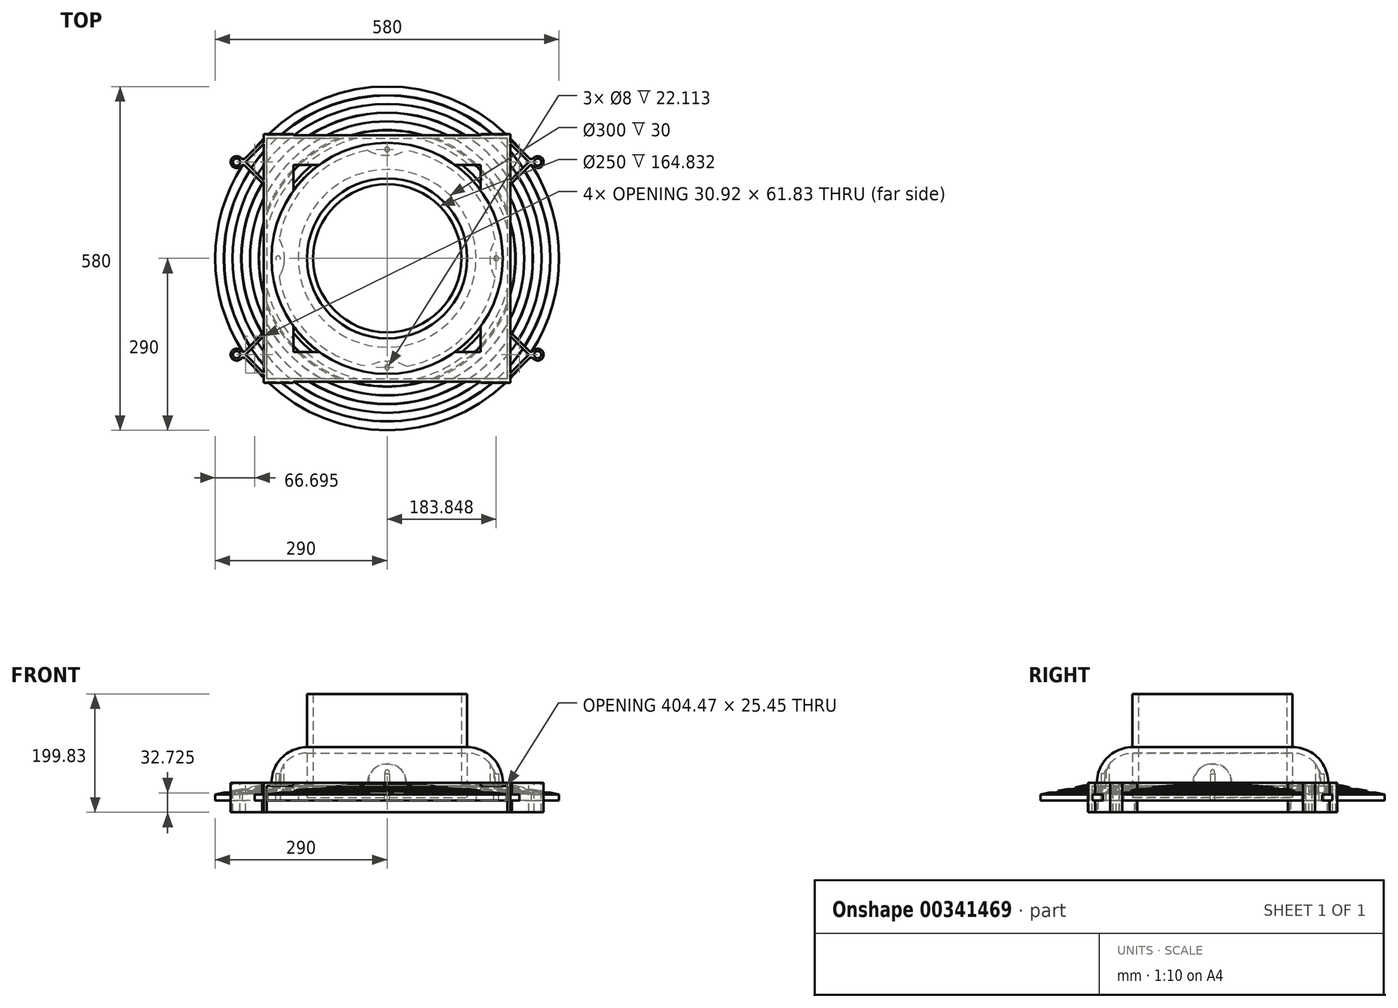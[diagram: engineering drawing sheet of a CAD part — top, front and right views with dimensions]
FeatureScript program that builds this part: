
annotation { "Feature Type Name" : "Feature", "Feature Type Description" : "" }
export const myFeature = defineFeature(function(context is Context, id is Id, definition is map)
    precondition{}
    {
        {
            var Q0;
            Q0=qCreatedBy(makeId("Top.planeOp"),FACE);
            var sketch = newSketch(context, id + "F0", { "sketchPlane" : qUnion([Q0])});
            skCircle(sketch, "E0", {"center": v(0, 0) * mm, "radius": 195 * mm});
            skCircle(sketch, "E1", {"center": v(0, 0) * mm, "radius": 135 * mm});
            skCircle(sketch, "E2", {"center": v(-183.85, 0) * mm, "radius": 4 * mm});
            skCircle(sketch, "E3", {"center": v(0, -183.85) * mm, "radius": 4 * mm});
            skCircle(sketch, "E4", {"center": v(183.85, 0) * mm, "radius": 4 * mm});
            skCircle(sketch, "E5", {"center": v(0, 183.85) * mm, "radius": 4 * mm});
            skFitSpline(sketch, "E6.MirrorCS", {"points": [v(-182.1, 32.59) * mm, v(-173.85, 0) * mm, v(-182.37, -31.1) * mm], "startDerivative": vector(43.9, -86.79) * mm, "endDerivative": vector(-46.42, -79.56) * mm});
            skArc(sketch, "E7.trimOffspring", {"start": v(-182.1, 32.59) * mm, "mid": v(-185, 0.76) * mm, "end": v(-182.37, -31.1) * mm});
            skArc(sketch, "E8.MirrorCS", {"start": v(32.59, -182.1) * mm, "mid": v(0.76, -185) * mm, "end": v(-31.1, -182.37) * mm});
            skFitSpline(sketch, "E9.MirrorCS", {"points": [v(32.59, -182.1) * mm, v(0, -173.85) * mm, v(-31.1, -182.37) * mm], "startDerivative": vector(-86.79, 43.9) * mm, "endDerivative": vector(-79.56, -46.42) * mm});
            skFitSpline(sketch, "E10.MirrorCS", {"points": [v(-32.59, 182.1) * mm, v(0, 173.85) * mm, v(31.1, 182.37) * mm], "startDerivative": vector(86.79, -43.9) * mm, "endDerivative": vector(79.56, 46.42) * mm});
            skArc(sketch, "E11.MirrorCS", {"start": v(-32.59, 182.1) * mm, "mid": v(-0.76, 185) * mm, "end": v(31.1, 182.37) * mm});
            skFitSpline(sketch, "E12.MirrorCS", {"points": [v(182.1, -32.59) * mm, v(173.85, 0) * mm, v(182.37, 31.1) * mm], "startDerivative": vector(-43.9, 86.79) * mm, "endDerivative": vector(46.42, 79.56) * mm});
            skArc(sketch, "E13.MirrorCS", {"start": v(182.1, -32.59) * mm, "mid": v(185, -0.76) * mm, "end": v(182.37, 31.1) * mm});
            skSolve(sketch);
        }
        {
            var Q0;
            Q0=qCreatedBy(makeId("Front.planeOp"),FACE);
            var sketch = newSketch(context, id + "F1", { "sketchPlane" : qUnion([Q0])});
            skLineSegment(sketch, "E14.top", {"start": v(195, 0) * mm, "end": v(185, 0) * mm});
            skLineSegment(sketch, "E15", {"start": v(135, -25) * mm, "end": v(135, 50) * mm});
            skLineSegment(sketch, "E16", {"start": v(185, 0) * mm, "end": v(135, 0) * mm, "construction": true});
            skArc(sketch, "E17", {"start": v(195, 0) * mm, "mid": v(177.43, 42.43) * mm, "end": v(135, 60) * mm});
            skArc(sketch, "E18", {"start": v(185, 0) * mm, "mid": v(170.36, 35.36) * mm, "end": v(135, 50) * mm});
            skLineSegment(sketch, "E19", {"start": v(135, 50) * mm, "end": v(135, 60) * mm, "construction": true});
            skLineSegment(sketch, "E20", {"start": v(135, 60) * mm, "end": v(135, 149.83) * mm});
            skLineSegment(sketch, "E21", {"start": v(135, 149.83) * mm, "end": v(125, 149.83) * mm});
            skLineSegment(sketch, "E22", {"start": v(125, 149.83) * mm, "end": v(125, -15) * mm});
            skLineSegment(sketch, "E23", {"start": v(0, -25) * mm, "end": v(135, -25) * mm});
            skLineSegment(sketch, "E24", {"start": v(0, -25) * mm, "end": v(0, -15) * mm});
            skLineSegment(sketch, "E25", {"start": v(0, -15) * mm, "end": v(125, -15) * mm});
            skSolve(sketch);
        }
        {
            var Q0;
            Q0=qSketchRegion(id+"F1",true);
            var Q1;
            Q1=sQuery(id+"F1.wireOp",EDGE,"E24");
            revolve(context, id + "F2", {"entities" : qUnion([Q0]), "axis" : qUnion([Q1]), "revolveType" : RevolveType.FULL});
        }
        {
            var Q0;
            {var subQ4=sQuery(id+"F0.wireOp",EDGE,"E6.MirrorCS");Q0=makeQuery(id+"F0.imprint","IMPRINT",FACE,{"disambiguationData":[TD([[makeQuery(id+"F0.imprint","IMPRINT",EDGE,{"derivedFrom":subQ4}),-1.0]])]});}
            var Q1;
            {var subQ0=sQuery(id+"F0.wireOp",EDGE,"E7.trimOffspring");var subQ1=sQuery(id+"F0.wireOp",EDGE,"E2");var subQ2=makeQuery(id+"F0.imprint","INTERSECT",VERTEX,{"disambiguationData":[OD(0.0)],"derivedFrom":[subQ1,subQ0]});Q1=makeQuery(id+"F0.imprint","IMPRINT",FACE,{"disambiguationData":[TD([[makeQuery(id+"F0.imprint","IMPRINT",EDGE,{"disambiguationData":[TD([[subQ2,1.0]])],"derivedFrom":subQ1}),1.0]])]});}
            var Q2;
            {var subQ4=sQuery(id+"F0.wireOp",EDGE,"E9.MirrorCS");Q2=makeQuery(id+"F0.imprint","IMPRINT",FACE,{"disambiguationData":[TD([[makeQuery(id+"F0.imprint","IMPRINT",EDGE,{"derivedFrom":subQ4}),1.0]])]});}
            var Q3;
            {var subQ0=sQuery(id+"F0.wireOp",EDGE,"7527a271-581c-4256-96df-404e9d61ec270.MirrorCS");var subQ1=sQuery(id+"F0.wireOp",EDGE,"E3");var subQ2=makeQuery(id+"F0.imprint","INTERSECT",VERTEX,{"disambiguationData":[OD(0.0)],"derivedFrom":[subQ1,subQ0]});Q3=makeQuery(id+"F0.imprint","IMPRINT",FACE,{"disambiguationData":[TD([[makeQuery(id+"F0.imprint","IMPRINT",EDGE,{"disambiguationData":[TD([[subQ2,-1.0]])],"derivedFrom":subQ1}),1.0]])]});}
            var Q4;
            {var subQ4=sQuery(id+"F0.wireOp",EDGE,"E12.MirrorCS");Q4=makeQuery(id+"F0.imprint","IMPRINT",FACE,{"disambiguationData":[TD([[makeQuery(id+"F0.imprint","IMPRINT",EDGE,{"derivedFrom":subQ4}),-1.0]])]});}
            var Q5;
            {var subQ0=sQuery(id+"F0.wireOp",EDGE,"E13.MirrorCS");var subQ1=sQuery(id+"F0.wireOp",EDGE,"E4");var subQ2=makeQuery(id+"F0.imprint","INTERSECT",VERTEX,{"disambiguationData":[OD(0.0)],"derivedFrom":[subQ1,subQ0]});Q5=makeQuery(id+"F0.imprint","IMPRINT",FACE,{"disambiguationData":[TD([[makeQuery(id+"F0.imprint","IMPRINT",EDGE,{"disambiguationData":[TD([[subQ2,1.0]])],"derivedFrom":subQ1}),1.0]])]});}
            var Q6;
            {var subQ4=sQuery(id+"F0.wireOp",EDGE,"E10.MirrorCS");Q6=makeQuery(id+"F0.imprint","IMPRINT",FACE,{"disambiguationData":[TD([[makeQuery(id+"F0.imprint","IMPRINT",EDGE,{"derivedFrom":subQ4}),1.0]])]});}
            var Q7;
            {var subQ0=sQuery(id+"F0.wireOp",EDGE,"E11.MirrorCS");var subQ1=sQuery(id+"F0.wireOp",EDGE,"E5");var subQ2=makeQuery(id+"F0.imprint","INTERSECT",VERTEX,{"disambiguationData":[OD(0.0)],"derivedFrom":[subQ1,subQ0]});Q7=makeQuery(id+"F0.imprint","IMPRINT",FACE,{"disambiguationData":[TD([[makeQuery(id+"F0.imprint","IMPRINT",EDGE,{"disambiguationData":[TD([[subQ2,-1.0]])],"derivedFrom":subQ1}),1.0]])]});}
            extrude(context, id + "F3", {"entities" : qUnion([Q0, Q1, Q2, Q3, Q4, Q5, Q6, Q7]), "operationType" : NewBodyOperationType.ADD, "endBound" : BoundingType.UP_TO_NEXT, "depth" : 100 * mm});
        }
        {
            var Q0;
            {var subQ0=sQuery(id+"F0.wireOp",EDGE,"E7.trimOffspring");var subQ1=sQuery(id+"F0.wireOp",EDGE,"E2");var subQ2=makeQuery(id+"F0.imprint","INTERSECT",VERTEX,{"disambiguationData":[OD(0.0)],"derivedFrom":[subQ1,subQ0]});Q0=makeQuery(id+"F0.imprint","IMPRINT",FACE,{"disambiguationData":[TD([[makeQuery(id+"F0.imprint","IMPRINT",EDGE,{"disambiguationData":[TD([[subQ2,1.0]])],"derivedFrom":subQ1}),1.0]])]});}
            var Q1;
            {var subQ0=sQuery(id+"F0.wireOp",EDGE,"E7.trimOffspring");var subQ1=sQuery(id+"F0.wireOp",EDGE,"E2");var subQ2=makeQuery(id+"F0.imprint","INTERSECT",VERTEX,{"disambiguationData":[OD(0.0)],"derivedFrom":[subQ1,subQ0]});Q1=makeQuery(id+"F0.imprint","IMPRINT",FACE,{"disambiguationData":[TD([[makeQuery(id+"F0.imprint","IMPRINT",EDGE,{"disambiguationData":[TD([[subQ2,-1.0]])],"derivedFrom":subQ1}),1.0]])]});}
            var Q2;
            {var subQ0=sQuery(id+"F0.wireOp",EDGE,"7527a271-581c-4256-96df-404e9d61ec270.MirrorCS");var subQ1=sQuery(id+"F0.wireOp",EDGE,"E3");var subQ2=makeQuery(id+"F0.imprint","INTERSECT",VERTEX,{"disambiguationData":[OD(0.0)],"derivedFrom":[subQ1,subQ0]});Q2=makeQuery(id+"F0.imprint","IMPRINT",FACE,{"disambiguationData":[TD([[makeQuery(id+"F0.imprint","IMPRINT",EDGE,{"disambiguationData":[TD([[subQ2,-1.0]])],"derivedFrom":subQ1}),1.0]])]});}
            var Q3;
            {var subQ0=sQuery(id+"F0.wireOp",EDGE,"7527a271-581c-4256-96df-404e9d61ec270.MirrorCS");var subQ1=sQuery(id+"F0.wireOp",EDGE,"E3");var subQ2=makeQuery(id+"F0.imprint","INTERSECT",VERTEX,{"disambiguationData":[OD(0.0)],"derivedFrom":[subQ1,subQ0]});Q3=makeQuery(id+"F0.imprint","IMPRINT",FACE,{"disambiguationData":[TD([[makeQuery(id+"F0.imprint","IMPRINT",EDGE,{"disambiguationData":[TD([[subQ2,1.0]])],"derivedFrom":subQ1}),1.0]])]});}
            var Q4;
            {var subQ0=sQuery(id+"F0.wireOp",EDGE,"E13.MirrorCS");var subQ1=sQuery(id+"F0.wireOp",EDGE,"E4");var subQ2=makeQuery(id+"F0.imprint","INTERSECT",VERTEX,{"disambiguationData":[OD(0.0)],"derivedFrom":[subQ1,subQ0]});Q4=makeQuery(id+"F0.imprint","IMPRINT",FACE,{"disambiguationData":[TD([[makeQuery(id+"F0.imprint","IMPRINT",EDGE,{"disambiguationData":[TD([[subQ2,-1.0]])],"derivedFrom":subQ1}),1.0]])]});}
            var Q5;
            {var subQ0=sQuery(id+"F0.wireOp",EDGE,"E13.MirrorCS");var subQ1=sQuery(id+"F0.wireOp",EDGE,"E4");var subQ2=makeQuery(id+"F0.imprint","INTERSECT",VERTEX,{"disambiguationData":[OD(0.0)],"derivedFrom":[subQ1,subQ0]});Q5=makeQuery(id+"F0.imprint","IMPRINT",FACE,{"disambiguationData":[TD([[makeQuery(id+"F0.imprint","IMPRINT",EDGE,{"disambiguationData":[TD([[subQ2,1.0]])],"derivedFrom":subQ1}),1.0]])]});}
            var Q6;
            {var subQ0=sQuery(id+"F0.wireOp",EDGE,"E11.MirrorCS");var subQ1=sQuery(id+"F0.wireOp",EDGE,"E5");var subQ2=makeQuery(id+"F0.imprint","INTERSECT",VERTEX,{"disambiguationData":[OD(0.0)],"derivedFrom":[subQ1,subQ0]});Q6=makeQuery(id+"F0.imprint","IMPRINT",FACE,{"disambiguationData":[TD([[makeQuery(id+"F0.imprint","IMPRINT",EDGE,{"disambiguationData":[TD([[subQ2,1.0]])],"derivedFrom":subQ1}),1.0]])]});}
            var Q7;
            {var subQ0=sQuery(id+"F0.wireOp",EDGE,"E11.MirrorCS");var subQ1=sQuery(id+"F0.wireOp",EDGE,"E5");var subQ2=makeQuery(id+"F0.imprint","INTERSECT",VERTEX,{"disambiguationData":[OD(0.0)],"derivedFrom":[subQ1,subQ0]});Q7=makeQuery(id+"F0.imprint","IMPRINT",FACE,{"disambiguationData":[TD([[makeQuery(id+"F0.imprint","IMPRINT",EDGE,{"disambiguationData":[TD([[subQ2,-1.0]])],"derivedFrom":subQ1}),1.0]])]});}
            var Q8;
            Q8=sQuery(id+"F0.wireOp",EDGE,"E2");
            extrude(context, id + "F4", {"entities" : qUnion([Q0, Q1, Q2, Q3, Q4, Q5, Q6, Q7]), "operationType" : NewBodyOperationType.REMOVE, "surfaceEntities" : qUnion([Q8]), "depth" : 15 * mm});
        }
        {
            var Q0;
            Q0=qCreatedBy(makeId("Top.planeOp"),FACE);
            var sketch = newSketch(context, id + "F5", { "sketchPlane" : qUnion([Q0])});
            skLineSegment(sketch, "E26.bottom", {"start": v(-207.85, 210) * mm, "end": v(-157.85, 210) * mm});
            skLineSegment(sketch, "E26.top", {"start": v(-207.85, -210) * mm, "end": v(-157.85, -210) * mm});
            skLineSegment(sketch, "E26.left", {"start": v(-207.85, 210) * mm, "end": v(-207.85, -210) * mm});
            skLineSegment(sketch, "E26.right", {"start": v(-157.85, 210) * mm, "end": v(-157.85, 207.85) * mm});
            skLineSegment(sketch, "E27.trimOffspring", {"start": v(-157.85, 0) * mm, "end": v(-157.85, -157.85) * mm});
            skLineSegment(sketch, "E28.MirrorCS", {"start": v(207.85, 210) * mm, "end": v(207.85, -210) * mm});
            skLineSegment(sketch, "E29.MirrorCS", {"start": v(157.85, 210) * mm, "end": v(157.85, 207.85) * mm});
            skLineSegment(sketch, "E30.MirrorCS", {"start": v(207.85, 210) * mm, "end": v(157.85, 210) * mm});
            skLineSegment(sketch, "E31.MirrorCS", {"start": v(207.85, -210) * mm, "end": v(157.85, -210) * mm});
            skLineSegment(sketch, "E32.MirrorCS", {"start": v(157.85, 0) * mm, "end": v(157.85, -157.85) * mm});
            skLineSegment(sketch, "E33", {"start": v(-157.85, 157.85) * mm, "end": v(0, 157.85) * mm});
            skLineSegment(sketch, "E34", {"start": v(-157.85, 207.85) * mm, "end": v(157.85, 207.85) * mm});
            skLineSegment(sketch, "E35.trimOffspring", {"start": v(-157.85, 157.85) * mm, "end": v(-157.85, 0) * mm});
            skLineSegment(sketch, "E36.trimOffspring", {"start": v(157.85, 157.85) * mm, "end": v(157.85, 0) * mm});
            skLineSegment(sketch, "E37", {"start": v(-157.85, -207.85) * mm, "end": v(157.85, -207.85) * mm});
            skLineSegment(sketch, "E38", {"start": v(-157.85, -157.85) * mm, "end": v(0, -157.85) * mm});
            skLineSegment(sketch, "E39.trimOffspring", {"start": v(-157.85, -207.85) * mm, "end": v(-157.85, -210) * mm});
            skLineSegment(sketch, "E40.trimOffspring", {"start": v(157.85, -207.85) * mm, "end": v(157.85, -210) * mm});
            skLineSegment(sketch, "E41", {"start": v(-157.85, 157.85) * mm, "end": v(-157.85, 207.85) * mm, "construction": true});
            skLineSegment(sketch, "E42", {"start": v(-157.85, -157.85) * mm, "end": v(-157.85, -207.85) * mm, "construction": true});
            skLineSegment(sketch, "E43.trimOffspring", {"start": v(0, 157.85) * mm, "end": v(157.85, 157.85) * mm});
            skLineSegment(sketch, "E44.trimOffspring", {"start": v(0, -157.85) * mm, "end": v(157.85, -157.85) * mm});
            skPoint(sketch, "E45.orphan", {"position": v(157.85, 0) * mm});
            skSolve(sketch);
        }
        {
            var Q0;
            Q0=makeQuery(id+"F5.imprint","IMPRINT",FACE,{"disambiguationData":[TD([[makeQuery(id+"F5.imprint","IMPRINT",EDGE,{"derivedFrom":sQuery(id+"F5.wireOp",EDGE,"E26.bottom")}),-1.0]])]});
            extrude(context, id + "F6", {"entities" : qUnion([Q0]), "oppositeDirection" : true, "depth" : 5 * mm});
        }
        {
            var Q0;
            Q0=makeQuery(id+"F6.opExtrude","CAP_FACE",FACE,{"disambiguationData":[OSD([sQuery(id+"F5.wireOp",EDGE,"E26.bottom"),sQuery(id+"F5.wireOp",EDGE,"E26.top"),sQuery(id+"F5.wireOp",EDGE,"E26.left"),sQuery(id+"F5.wireOp",EDGE,"E26.right"),sQuery(id+"F5.wireOp",EDGE,"E27.trimOffspring"),sQuery(id+"F5.wireOp",EDGE,"E28.MirrorCS"),sQuery(id+"F5.wireOp",EDGE,"E29.MirrorCS"),sQuery(id+"F5.wireOp",EDGE,"E30.MirrorCS"),sQuery(id+"F5.wireOp",EDGE,"E31.MirrorCS"),sQuery(id+"F5.wireOp",EDGE,"E32.MirrorCS"),sQuery(id+"F5.wireOp",EDGE,"1075a56e-54ef-4c14-a711-8a0c5d75a75e0.MirrorCS"),sQuery(id+"F5.wireOp",EDGE,"E33"),sQuery(id+"F5.wireOp",EDGE,"E34"),sQuery(id+"F5.wireOp",EDGE,"E35.trimOffspring"),sQuery(id+"F5.wireOp",EDGE,"E36.trimOffspring"),sQuery(id+"F5.wireOp",EDGE,"E37"),sQuery(id+"F5.wireOp",EDGE,"E38"),sQuery(id+"F5.wireOp",EDGE,"E39.trimOffspring"),sQuery(id+"F5.wireOp",EDGE,"E40.trimOffspring"),sQuery(id+"F5.wireOp",EDGE,"E43.trimOffspring"),sQuery(id+"F5.wireOp",EDGE,"E44.trimOffspring"),sQuery(id+"F5.wireOp",EDGE,"631d3be9-6cdb-41e6-bc76-cfa904feda63.trimOffspring"),sQuery(id+"F5.wireOp",EDGE,"dfcaf6fc-a254-42b6-abba-36afba2b6a58.trimOffspring"),sQuery(id+"F5.wireOp",EDGE,"64f1b304-52c1-49c5-a0df-f42b03db2a1c.trimOffspring")])],"isStart":false});
            var sketch = newSketch(context, id + "F7", { "sketchPlane" : qUnion([Q0])});
            skLineSegment(sketch, "E46.bottom", {"start": v(207.85, 210) * mm, "end": v(202.85, 210) * mm});
            skLineSegment(sketch, "E46.top", {"start": v(207.85, -210) * mm, "end": v(202.85, -210) * mm});
            skLineSegment(sketch, "E46.left", {"start": v(207.85, 210) * mm, "end": v(207.85, -210) * mm});
            skLineSegment(sketch, "E46.right", {"start": v(202.85, 210) * mm, "end": v(202.85, -210) * mm});
            skLineSegment(sketch, "E47.bottom", {"start": v(-207.85, 210) * mm, "end": v(-202.85, 210) * mm});
            skLineSegment(sketch, "E47.top", {"start": v(-207.85, -210) * mm, "end": v(-202.85, -210) * mm});
            skLineSegment(sketch, "E47.left", {"start": v(-207.85, 210) * mm, "end": v(-207.85, -210) * mm});
            skLineSegment(sketch, "E47.right", {"start": v(-202.85, 210) * mm, "end": v(-202.85, -210) * mm});
            skLineSegment(sketch, "E48.bottom", {"start": v(202.85, -207.85) * mm, "end": v(-202.85, -207.85) * mm});
            skLineSegment(sketch, "E48.top", {"start": v(202.85, -202.85) * mm, "end": v(-202.85, -202.85) * mm});
            skLineSegment(sketch, "E48.left", {"start": v(202.85, -207.85) * mm, "end": v(202.85, -202.85) * mm});
            skLineSegment(sketch, "E48.right", {"start": v(-202.85, -207.85) * mm, "end": v(-202.85, -202.85) * mm});
            skLineSegment(sketch, "E49.bottom", {"start": v(202.85, 207.85) * mm, "end": v(-202.85, 207.85) * mm});
            skLineSegment(sketch, "E49.top", {"start": v(202.85, 202.85) * mm, "end": v(-202.85, 202.85) * mm});
            skLineSegment(sketch, "E49.left", {"start": v(202.85, 207.85) * mm, "end": v(202.85, 202.85) * mm});
            skLineSegment(sketch, "E49.right", {"start": v(-202.85, 207.85) * mm, "end": v(-202.85, 202.85) * mm});
            skSolve(sketch);
        }
        {
            var Q0;
            {var subQ1=sQuery(id+"F7.wireOp",EDGE,"E46.bottom");Q0=makeQuery(id+"F7.imprint","IMPRINT",FACE,{"disambiguationData":[TD([[makeQuery(id+"F7.imprint","IMPRINT",EDGE,{"derivedFrom":subQ1}),1.0]])]});}
            var Q1;
            Q1=makeQuery(id+"F7.imprint","IMPRINT",FACE,{"disambiguationData":[TD([[makeQuery(id+"F7.imprint","IMPRINT",EDGE,{"derivedFrom":sQuery(id+"F7.wireOp",EDGE,"E49.top")}),-1.0]])]});
            var Q2;
            Q2=makeQuery(id+"F7.imprint","IMPRINT",FACE,{"disambiguationData":[TD([[makeQuery(id+"F7.imprint","IMPRINT",EDGE,{"derivedFrom":sQuery(id+"F7.wireOp",EDGE,"E48.top")}),1.0]])]});
            var Q3;
            {var subQ1=sQuery(id+"F7.wireOp",EDGE,"E47.bottom");Q3=makeQuery(id+"F7.imprint","IMPRINT",FACE,{"disambiguationData":[TD([[makeQuery(id+"F7.imprint","IMPRINT",EDGE,{"derivedFrom":subQ1}),-1.0]])]});}
            extrude(context, id + "F8", {"entities" : qUnion([Q0, Q1, Q2, Q3]), "operationType" : NewBodyOperationType.ADD, "depth" : 45 * mm});
        }
        {
            var Q0;
            {var subQ0=sQuery(id+"F0.wireOp",EDGE,"E7.trimOffspring");var subQ1=sQuery(id+"F0.wireOp",EDGE,"E2");var subQ2=makeQuery(id+"F0.imprint","INTERSECT",VERTEX,{"disambiguationData":[OD(0.0)],"derivedFrom":[subQ1,subQ0]});Q0=makeQuery(id+"F0.imprint","IMPRINT",FACE,{"disambiguationData":[TD([[makeQuery(id+"F0.imprint","IMPRINT",EDGE,{"disambiguationData":[TD([[subQ2,-1.0]])],"derivedFrom":subQ1}),1.0]])]});}
            var Q1;
            {var subQ0=sQuery(id+"F0.wireOp",EDGE,"E7.trimOffspring");var subQ1=sQuery(id+"F0.wireOp",EDGE,"E2");var subQ2=makeQuery(id+"F0.imprint","INTERSECT",VERTEX,{"disambiguationData":[OD(0.0)],"derivedFrom":[subQ1,subQ0]});Q1=makeQuery(id+"F0.imprint","IMPRINT",FACE,{"disambiguationData":[TD([[makeQuery(id+"F0.imprint","IMPRINT",EDGE,{"disambiguationData":[TD([[subQ2,1.0]])],"derivedFrom":subQ1}),1.0]])]});}
            var Q2;
            {var subQ0=sQuery(id+"F0.wireOp",EDGE,"7527a271-581c-4256-96df-404e9d61ec270.MirrorCS");var subQ1=sQuery(id+"F0.wireOp",EDGE,"E3");var subQ2=makeQuery(id+"F0.imprint","INTERSECT",VERTEX,{"disambiguationData":[OD(0.0)],"derivedFrom":[subQ1,subQ0]});Q2=makeQuery(id+"F0.imprint","IMPRINT",FACE,{"disambiguationData":[TD([[makeQuery(id+"F0.imprint","IMPRINT",EDGE,{"disambiguationData":[TD([[subQ2,-1.0]])],"derivedFrom":subQ1}),1.0]])]});}
            var Q3;
            {var subQ0=sQuery(id+"F0.wireOp",EDGE,"7527a271-581c-4256-96df-404e9d61ec270.MirrorCS");var subQ1=sQuery(id+"F0.wireOp",EDGE,"E3");var subQ2=makeQuery(id+"F0.imprint","INTERSECT",VERTEX,{"disambiguationData":[OD(0.0)],"derivedFrom":[subQ1,subQ0]});Q3=makeQuery(id+"F0.imprint","IMPRINT",FACE,{"disambiguationData":[TD([[makeQuery(id+"F0.imprint","IMPRINT",EDGE,{"disambiguationData":[TD([[subQ2,1.0]])],"derivedFrom":subQ1}),1.0]])]});}
            var Q4;
            {var subQ0=sQuery(id+"F0.wireOp",EDGE,"E13.MirrorCS");var subQ1=sQuery(id+"F0.wireOp",EDGE,"E4");var subQ2=makeQuery(id+"F0.imprint","INTERSECT",VERTEX,{"disambiguationData":[OD(0.0)],"derivedFrom":[subQ1,subQ0]});Q4=makeQuery(id+"F0.imprint","IMPRINT",FACE,{"disambiguationData":[TD([[makeQuery(id+"F0.imprint","IMPRINT",EDGE,{"disambiguationData":[TD([[subQ2,-1.0]])],"derivedFrom":subQ1}),1.0]])]});}
            var Q5;
            {var subQ0=sQuery(id+"F0.wireOp",EDGE,"E13.MirrorCS");var subQ1=sQuery(id+"F0.wireOp",EDGE,"E4");var subQ2=makeQuery(id+"F0.imprint","INTERSECT",VERTEX,{"disambiguationData":[OD(0.0)],"derivedFrom":[subQ1,subQ0]});Q5=makeQuery(id+"F0.imprint","IMPRINT",FACE,{"disambiguationData":[TD([[makeQuery(id+"F0.imprint","IMPRINT",EDGE,{"disambiguationData":[TD([[subQ2,1.0]])],"derivedFrom":subQ1}),1.0]])]});}
            var Q6;
            {var subQ0=sQuery(id+"F0.wireOp",EDGE,"E11.MirrorCS");var subQ1=sQuery(id+"F0.wireOp",EDGE,"E5");var subQ2=makeQuery(id+"F0.imprint","INTERSECT",VERTEX,{"disambiguationData":[OD(0.0)],"derivedFrom":[subQ1,subQ0]});Q6=makeQuery(id+"F0.imprint","IMPRINT",FACE,{"disambiguationData":[TD([[makeQuery(id+"F0.imprint","IMPRINT",EDGE,{"disambiguationData":[TD([[subQ2,1.0]])],"derivedFrom":subQ1}),1.0]])]});}
            var Q7;
            {var subQ0=sQuery(id+"F0.wireOp",EDGE,"E11.MirrorCS");var subQ1=sQuery(id+"F0.wireOp",EDGE,"E5");var subQ2=makeQuery(id+"F0.imprint","INTERSECT",VERTEX,{"disambiguationData":[OD(0.0)],"derivedFrom":[subQ1,subQ0]});Q7=makeQuery(id+"F0.imprint","IMPRINT",FACE,{"disambiguationData":[TD([[makeQuery(id+"F0.imprint","IMPRINT",EDGE,{"disambiguationData":[TD([[subQ2,-1.0]])],"derivedFrom":subQ1}),1.0]])]});}
            extrude(context, id + "F9", {"entities" : qUnion([Q0, Q1, Q2, Q3, Q4, Q5, Q6, Q7]), "operationType" : NewBodyOperationType.REMOVE, "endBound" : BoundingType.THROUGH_ALL, "oppositeDirection" : true, "depth" : 25 * mm});
        }
        {
            var Q0;
            Q0=qCreatedBy(makeId("Front.planeOp"),FACE);
            var sketch = newSketch(context, id + "F10", { "sketchPlane" : qUnion([Q0])});
            skLineSegment(sketch, "E50", {"start": v(195, 0) * mm, "end": v(201.93, -1.46) * mm});
            skLineSegment(sketch, "E51", {"start": v(290, -20) * mm, "end": v(290, -30) * mm});
            skLineSegment(sketch, "E52", {"start": v(290, -30) * mm, "end": v(150, -30) * mm});
            skLineSegment(sketch, "E53", {"start": v(150, -30) * mm, "end": v(150, 0) * mm});
            skLineSegment(sketch, "E54", {"start": v(201.93, -1.46) * mm, "end": v(201.52, -3.42) * mm});
            skLineSegment(sketch, "E55", {"start": v(201.52, -3.42) * mm, "end": v(216.2, -6.5) * mm});
            skLineSegment(sketch, "E56", {"start": v(216.2, -6.5) * mm, "end": v(216.6, -4.55) * mm});
            skLineSegment(sketch, "E57", {"start": v(231.29, -7.64) * mm, "end": v(230.87, -9.6) * mm});
            skLineSegment(sketch, "E58", {"start": v(230.87, -9.6) * mm, "end": v(245.55, -12.69) * mm});
            skLineSegment(sketch, "E59", {"start": v(245.55, -12.69) * mm, "end": v(245.97, -10.73) * mm});
            skLineSegment(sketch, "E60", {"start": v(260.64, -13.82) * mm, "end": v(260.23, -15.78) * mm});
            skLineSegment(sketch, "E61", {"start": v(260.23, -15.78) * mm, "end": v(274.9, -18.87) * mm});
            skLineSegment(sketch, "E62", {"start": v(274.9, -18.87) * mm, "end": v(275.32, -16.9) * mm});
            skLineSegment(sketch, "E63.trimOffspring", {"start": v(216.6, -4.55) * mm, "end": v(231.29, -7.64) * mm});
            skLineSegment(sketch, "E64.trimOffspring", {"start": v(245.97, -10.73) * mm, "end": v(260.64, -13.82) * mm});
            skLineSegment(sketch, "E65.trimOffspring", {"start": v(275.32, -16.9) * mm, "end": v(290, -20) * mm});
            skLineSegment(sketch, "E66", {"start": v(150, 0) * mm, "end": v(195, 0) * mm});
            skSolve(sketch);
        }
        {
            var Q0;
            Q0=makeQuery(id+"F10.imprint","IMPRINT",FACE,{"disambiguationData":[TD([[makeQuery(id+"F10.imprint","IMPRINT",EDGE,{"derivedFrom":sQuery(id+"F10.wireOp",EDGE,"E50")}),-1.0]])]});
            var Q1;
            Q1=sQuery(id+"F1.wireOp",EDGE,"E24");
            revolve(context, id + "F11", {"entities" : qUnion([Q0]), "axis" : qUnion([Q1]), "revolveType" : RevolveType.FULL});
        }
        {
            var Q0;
            {var subQ0=sQuery(id+"F0.wireOp",EDGE,"E11.MirrorCS");var subQ1=sQuery(id+"F0.wireOp",EDGE,"E5");var subQ2=makeQuery(id+"F0.imprint","INTERSECT",VERTEX,{"disambiguationData":[OD(0.0)],"derivedFrom":[subQ1,subQ0]});Q0=makeQuery(id+"F0.imprint","IMPRINT",FACE,{"disambiguationData":[TD([[makeQuery(id+"F0.imprint","IMPRINT",EDGE,{"disambiguationData":[TD([[subQ2,-1.0]])],"derivedFrom":subQ1}),1.0]])]});}
            var Q1;
            {var subQ0=sQuery(id+"F0.wireOp",EDGE,"E13.MirrorCS");var subQ1=sQuery(id+"F0.wireOp",EDGE,"E4");var subQ2=makeQuery(id+"F0.imprint","INTERSECT",VERTEX,{"disambiguationData":[OD(0.0)],"derivedFrom":[subQ1,subQ0]});Q1=makeQuery(id+"F0.imprint","IMPRINT",FACE,{"disambiguationData":[TD([[makeQuery(id+"F0.imprint","IMPRINT",EDGE,{"disambiguationData":[TD([[subQ2,-1.0]])],"derivedFrom":subQ1}),1.0]])]});}
            var Q2;
            {var subQ0=sQuery(id+"F0.wireOp",EDGE,"E13.MirrorCS");var subQ1=sQuery(id+"F0.wireOp",EDGE,"E4");var subQ2=makeQuery(id+"F0.imprint","INTERSECT",VERTEX,{"disambiguationData":[OD(0.0)],"derivedFrom":[subQ1,subQ0]});Q2=makeQuery(id+"F0.imprint","IMPRINT",FACE,{"disambiguationData":[TD([[makeQuery(id+"F0.imprint","IMPRINT",EDGE,{"disambiguationData":[TD([[subQ2,1.0]])],"derivedFrom":subQ1}),1.0]])]});}
            var Q3;
            {var subQ0=sQuery(id+"F0.wireOp",EDGE,"7527a271-581c-4256-96df-404e9d61ec270.MirrorCS");var subQ1=sQuery(id+"F0.wireOp",EDGE,"E3");var subQ2=makeQuery(id+"F0.imprint","INTERSECT",VERTEX,{"disambiguationData":[OD(0.0)],"derivedFrom":[subQ1,subQ0]});Q3=makeQuery(id+"F0.imprint","IMPRINT",FACE,{"disambiguationData":[TD([[makeQuery(id+"F0.imprint","IMPRINT",EDGE,{"disambiguationData":[TD([[subQ2,-1.0]])],"derivedFrom":subQ1}),1.0]])]});}
            var Q4;
            {var subQ0=sQuery(id+"F0.wireOp",EDGE,"7527a271-581c-4256-96df-404e9d61ec270.MirrorCS");var subQ1=sQuery(id+"F0.wireOp",EDGE,"E3");var subQ2=makeQuery(id+"F0.imprint","INTERSECT",VERTEX,{"disambiguationData":[OD(0.0)],"derivedFrom":[subQ1,subQ0]});Q4=makeQuery(id+"F0.imprint","IMPRINT",FACE,{"disambiguationData":[TD([[makeQuery(id+"F0.imprint","IMPRINT",EDGE,{"disambiguationData":[TD([[subQ2,1.0]])],"derivedFrom":subQ1}),1.0]])]});}
            var Q5;
            {var subQ0=sQuery(id+"F0.wireOp",EDGE,"E7.trimOffspring");var subQ1=sQuery(id+"F0.wireOp",EDGE,"E2");var subQ2=makeQuery(id+"F0.imprint","INTERSECT",VERTEX,{"disambiguationData":[OD(0.0)],"derivedFrom":[subQ1,subQ0]});Q5=makeQuery(id+"F0.imprint","IMPRINT",FACE,{"disambiguationData":[TD([[makeQuery(id+"F0.imprint","IMPRINT",EDGE,{"disambiguationData":[TD([[subQ2,-1.0]])],"derivedFrom":subQ1}),1.0]])]});}
            var Q6;
            {var subQ0=sQuery(id+"F0.wireOp",EDGE,"E7.trimOffspring");var subQ1=sQuery(id+"F0.wireOp",EDGE,"E2");var subQ2=makeQuery(id+"F0.imprint","INTERSECT",VERTEX,{"disambiguationData":[OD(0.0)],"derivedFrom":[subQ1,subQ0]});Q6=makeQuery(id+"F0.imprint","IMPRINT",FACE,{"disambiguationData":[TD([[makeQuery(id+"F0.imprint","IMPRINT",EDGE,{"disambiguationData":[TD([[subQ2,1.0]])],"derivedFrom":subQ1}),1.0]])]});}
            var Q7;
            {var subQ0=sQuery(id+"F0.wireOp",EDGE,"E11.MirrorCS");var subQ1=sQuery(id+"F0.wireOp",EDGE,"E5");var subQ2=makeQuery(id+"F0.imprint","INTERSECT",VERTEX,{"disambiguationData":[OD(0.0)],"derivedFrom":[subQ1,subQ0]});Q7=makeQuery(id+"F0.imprint","IMPRINT",FACE,{"disambiguationData":[TD([[makeQuery(id+"F0.imprint","IMPRINT",EDGE,{"disambiguationData":[TD([[subQ2,1.0]])],"derivedFrom":subQ1}),1.0]])]});}
            extrude(context, id + "F12", {"entities" : qUnion([Q0, Q1, Q2, Q3, Q4, Q5, Q6, Q7]), "operationType" : NewBodyOperationType.REMOVE, "endBound" : BoundingType.THROUGH_ALL, "oppositeDirection" : true, "depth" : 25 * mm});
        }
        {
            var Q0;
            Q0=qCreatedBy(makeId("Top.planeOp"),FACE);
            var sketch = newSketch(context, id + "F13", { "sketchPlane" : qUnion([Q0])});
            skLineSegment(sketch, "E67", {"start": v(-210.48, 197.85) * mm, "end": v(-239.29, 169.04) * mm});
            skLineSegment(sketch, "E68", {"start": v(-239.29, 155.94) * mm, "end": v(-210.48, 127.14) * mm});
            skLineSegment(sketch, "E69", {"start": v(-210.48, 127.14) * mm, "end": v(-206.94, 130.67) * mm});
            skLineSegment(sketch, "E70", {"start": v(-206.94, 130.67) * mm, "end": v(-238.76, 162.5) * mm});
            skLineSegment(sketch, "E71", {"start": v(-238.76, 162.5) * mm, "end": v(-206.94, 194.31) * mm});
            skLineSegment(sketch, "E72", {"start": v(-206.94, 194.31) * mm, "end": v(-210.48, 197.85) * mm});
            skLineSegment(sketch, "E73", {"start": v(-245.83, 162.5) * mm, "end": v(-215.67, 162.5) * mm, "construction": true});
            skCircle(sketch, "E74", {"center": v(-253.93, 162.5) * mm, "radius": 6 * mm});
            skArc(sketch, "E75", {"start": v(-246.52, 169.22) * mm, "mid": v(-263.93, 162.5) * mm, "end": v(-246.52, 155.77) * mm});
            skLineSegment(sketch, "E76", {"start": v(-245.83, 162.5) * mm, "end": v(-276.4, 162.5) * mm, "construction": true});
            skPoint(sketch, "E77.visualSharp", {"position": v(-244.08, 164.25) * mm});
            skArc(sketch, "E77.filletArc", {"start": v(-246.52, 169.22) * mm, "mid": v(-242.94, 167.58) * mm, "end": v(-239.29, 169.04) * mm});
            skPoint(sketch, "E78.visualSharp", {"position": v(-244.08, 160.74) * mm});
            skArc(sketch, "E78.filletArc", {"start": v(-239.29, 155.94) * mm, "mid": v(-242.94, 157.4) * mm, "end": v(-246.52, 155.77) * mm});
            skSolve(sketch);
        }
        {
            var Q0;
            Q0=makeQuery(id+"F13.imprint","IMPRINT",FACE,{"disambiguationData":[TD([[makeQuery(id+"F13.imprint","IMPRINT",EDGE,{"derivedFrom":sQuery(id+"F13.wireOp",EDGE,"E67")}),1.0]])]});
            extrude(context, id + "F14", {"entities" : qUnion([Q0]), "oppositeDirection" : true, "depth" : 50 * mm});
        }
        {
            var Q0;
            Q0=makeQuery(id+"F14.opExtrude","SWEPT_BODY",BODY,{"disambiguationData":[OSD([sQuery(id+"F13.wireOp",EDGE,"E67"),sQuery(id+"F13.wireOp",EDGE,"E68"),sQuery(id+"F13.wireOp",EDGE,"E69"),sQuery(id+"F13.wireOp",EDGE,"E70"),sQuery(id+"F13.wireOp",EDGE,"E71"),sQuery(id+"F13.wireOp",EDGE,"E72"),sQuery(id+"F13.wireOp",EDGE,"E74"),sQuery(id+"F13.wireOp",EDGE,"E75"),sQuery(id+"F13.wireOp",EDGE,"E77.filletArc"),sQuery(id+"F13.wireOp",EDGE,"E78.filletArc")])]});
            var Q1;
            Q1=qCreatedBy(makeId("Right.planeOp"),FACE);
            mirror(context, id + "F15", {"entities" : qUnion([Q0]), "mirrorPlane" : qUnion([Q1])});
        }
        {
            var Q0;
            Q0=makeQuery(id+"F14.opExtrude","SWEPT_BODY",BODY,{"disambiguationData":[OSD([sQuery(id+"F13.wireOp",EDGE,"E67"),sQuery(id+"F13.wireOp",EDGE,"E68"),sQuery(id+"F13.wireOp",EDGE,"E69"),sQuery(id+"F13.wireOp",EDGE,"E70"),sQuery(id+"F13.wireOp",EDGE,"E71"),sQuery(id+"F13.wireOp",EDGE,"E72"),sQuery(id+"F13.wireOp",EDGE,"E74"),sQuery(id+"F13.wireOp",EDGE,"E75"),sQuery(id+"F13.wireOp",EDGE,"E77.filletArc"),sQuery(id+"F13.wireOp",EDGE,"E78.filletArc")])]});
            var Q1;
            Q1=makeQuery(id+"F15.opPattern","COPY",BODY,{"derivedFrom":makeQuery(id+"F14.opExtrude","SWEPT_BODY",BODY,{"disambiguationData":[OSD([sQuery(id+"F13.wireOp",EDGE,"E67"),sQuery(id+"F13.wireOp",EDGE,"E68"),sQuery(id+"F13.wireOp",EDGE,"E69"),sQuery(id+"F13.wireOp",EDGE,"E70"),sQuery(id+"F13.wireOp",EDGE,"E71"),sQuery(id+"F13.wireOp",EDGE,"E72"),sQuery(id+"F13.wireOp",EDGE,"E74"),sQuery(id+"F13.wireOp",EDGE,"E75"),sQuery(id+"F13.wireOp",EDGE,"E77.filletArc"),sQuery(id+"F13.wireOp",EDGE,"E78.filletArc")])]}),"instanceName":"1"});
            var Q2;
            Q2=qCreatedBy(makeId("Front.planeOp"),FACE);
            mirror(context, id + "F16", {"operationType" : NewBodyOperationType.ADD, "entities" : qUnion([Q0, Q1]), "mirrorPlane" : qUnion([Q2])});
        }
    });
